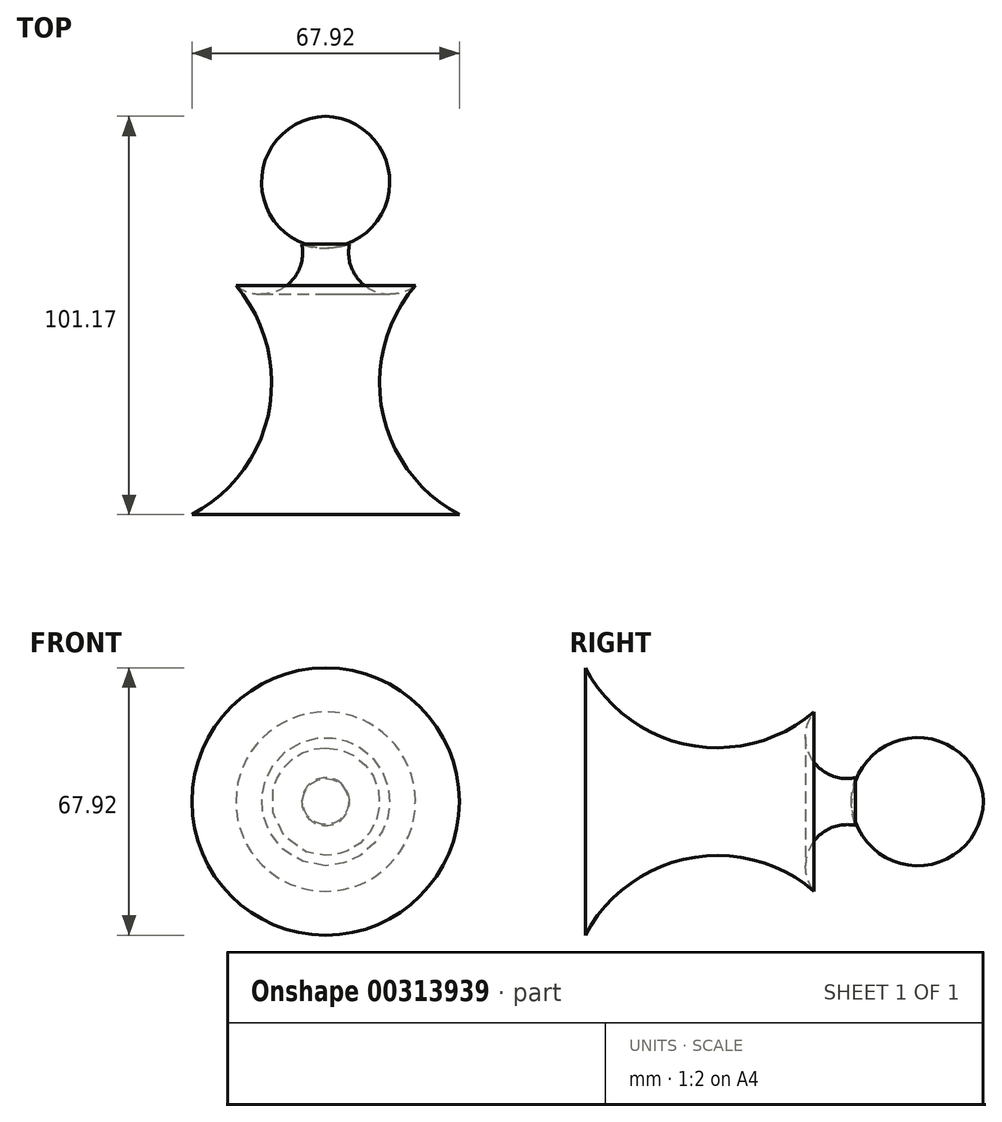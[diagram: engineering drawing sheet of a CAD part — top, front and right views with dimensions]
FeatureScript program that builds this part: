
annotation { "Feature Type Name" : "Feature", "Feature Type Description" : "" }
export const myFeature = defineFeature(function(context is Context, id is Id, definition is map)
    precondition{}
    {
        {
            var Q0;
            Q0=qCreatedBy(makeId("Top.planeOp"),FACE);
            var sketch = newSketch(context, id + "F0", { "sketchPlane" : qUnion([Q0])});
            skLineSegment(sketch, "E0", {"start": v(0, 56.75) * mm, "end": v(0, -44.42) * mm});
            skArc(sketch, "E1", {"start": v(0, 23.26) * mm, "mid": v(17.22, 40) * mm, "end": v(0, 56.75) * mm});
            skArc(sketch, "E2", {"start": v(6.07, 24.22) * mm, "mid": v(10.78, 13.16) * mm, "end": v(22.8, 13.72) * mm});
            skLineSegment(sketch, "E3", {"start": v(0, -44.42) * mm, "end": v(33.96, -44.42) * mm});
            skArc(sketch, "E4", {"start": v(22.8, 13.72) * mm, "mid": v(14.38, -18.04) * mm, "end": v(33.96, -44.42) * mm});
            skSolve(sketch);
        }
        {
            var Q0;
            {var subQ0=sQuery(id+"F0.wireOp",EDGE,"E1");var subQ1=sQuery(id+"F0.wireOp",EDGE,"E0");var subQ2=makeQuery(id+"F0.imprint","INTERSECT",VERTEX,{"disambiguationData":[OD(0.0)],"derivedFrom":[subQ1,subQ0]});Q0=makeQuery(id+"F0.imprint","IMPRINT",FACE,{"disambiguationData":[TD([[makeQuery(id+"F0.imprint","IMPRINT",EDGE,{"disambiguationData":[TD([[subQ2,-1.0]])],"derivedFrom":subQ1}),1.0]])]});}
            var Q1;
            {var subQ1=sQuery(id+"F0.wireOp",EDGE,"E2");Q1=makeQuery(id+"F0.imprint","IMPRINT",FACE,{"disambiguationData":[TD([[makeQuery(id+"F0.imprint","IMPRINT",EDGE,{"derivedFrom":subQ1}),-1.0]])]});}
            var Q2;
            Q2=sQuery(id+"F0.wireOp",EDGE,"E0");
            revolve(context, id + "F1", {"entities" : qUnion([Q0, Q1]), "axis" : qUnion([Q2]), "revolveType" : RevolveType.FULL});
        }
    });
